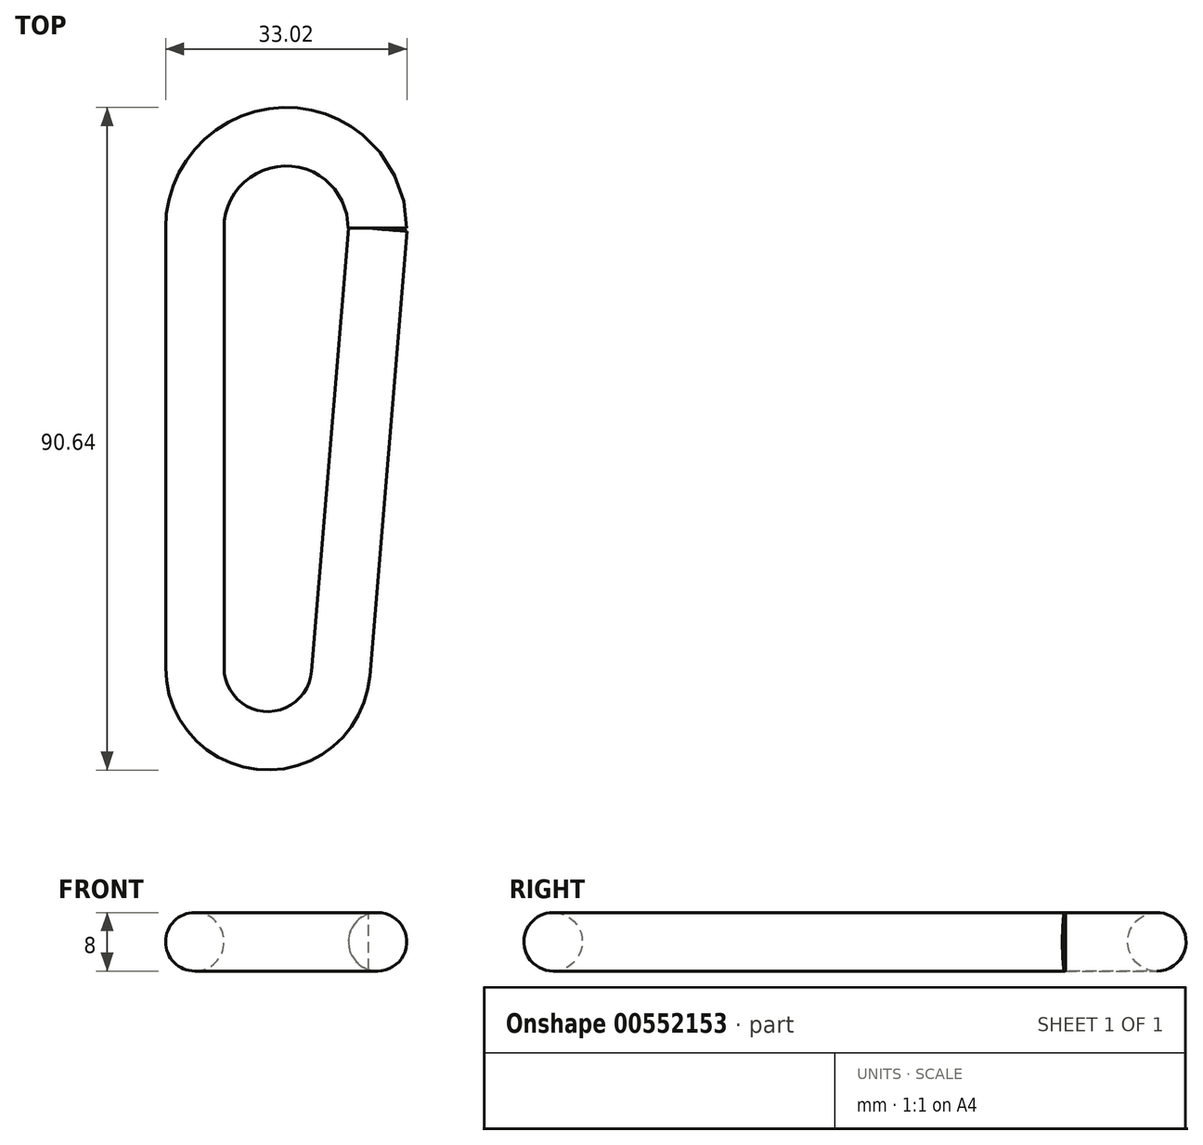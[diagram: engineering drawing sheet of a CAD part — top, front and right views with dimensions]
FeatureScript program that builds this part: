
annotation { "Feature Type Name" : "Feature", "Feature Type Description" : "" }
export const myFeature = defineFeature(function(context is Context, id is Id, definition is map)
    precondition{}
    {
        {
            var Q0;
            Q0=qCreatedBy(makeId("Top.planeOp"),FACE);
            var sketch = newSketch(context, id + "F0", { "sketchPlane" : qUnion([Q0])});
            skArc(sketch, "E0", {"start": v(15, 0) * mm, "mid": v(2.5, 12.5) * mm, "end": v(-10, 0) * mm});
            skArc(sketch, "E1", {"start": v(-10, -60.14) * mm, "mid": v(-0.42, -70.13) * mm, "end": v(9.97, -60.97) * mm});
            skLineSegment(sketch, "E2.bottom", {"start": v(0, 0) * mm, "end": v(0, 0) * mm});
            skLineSegment(sketch, "E2.top", {"start": v(2.5, -60) * mm, "end": v(2.5, -60) * mm});
            skLineSegment(sketch, "E2.left", {"start": v(0, 0) * mm, "end": v(0, -60) * mm, "construction": true});
            skLineSegment(sketch, "E2.right", {"start": v(0, 0) * mm, "end": v(0, -60) * mm, "construction": true});
            skLineSegment(sketch, "E3", {"start": v(15.03, -0.1) * mm, "end": v(9.97, -60.97) * mm});
            skLineSegment(sketch, "E4", {"start": v(-10, 0) * mm, "end": v(-10, -60.14) * mm});
            skSolve(sketch);
        }
        {
            var Q0;
            Q0=qCreatedBy(makeId("Front.planeOp"),FACE);
            var sketch = newSketch(context, id + "F1", { "sketchPlane" : qUnion([Q0])});
            skCircle(sketch, "E5", {"center": v(15, 0) * mm, "radius": 4 * mm});
            skSolve(sketch);
        }
        {
            var Q0;
            Q0=makeQuery(id+"F1.imprint","IMPRINT",FACE,{"disambiguationData":[TD([[makeQuery(id+"F1.imprint","IMPRINT",EDGE,{"derivedFrom":sQuery(id+"F1.wireOp",EDGE,"E5")}),1.0]])]});
            var Q1;
            Q1=sQuery(id+"F0.wireOp",EDGE,"E3");
            var Q2;
            Q2=sQuery(id+"F0.wireOp",EDGE,"E1");
            var Q3;
            Q3=sQuery(id+"F0.wireOp",EDGE,"E4");
            var Q4;
            Q4=sQuery(id+"F0.wireOp",EDGE,"E0");
            sweep(context, id + "F2", {"profiles" : qUnion([Q0]), "path" : qUnion([Q1, Q2, Q3, Q4])});
        }
    });
